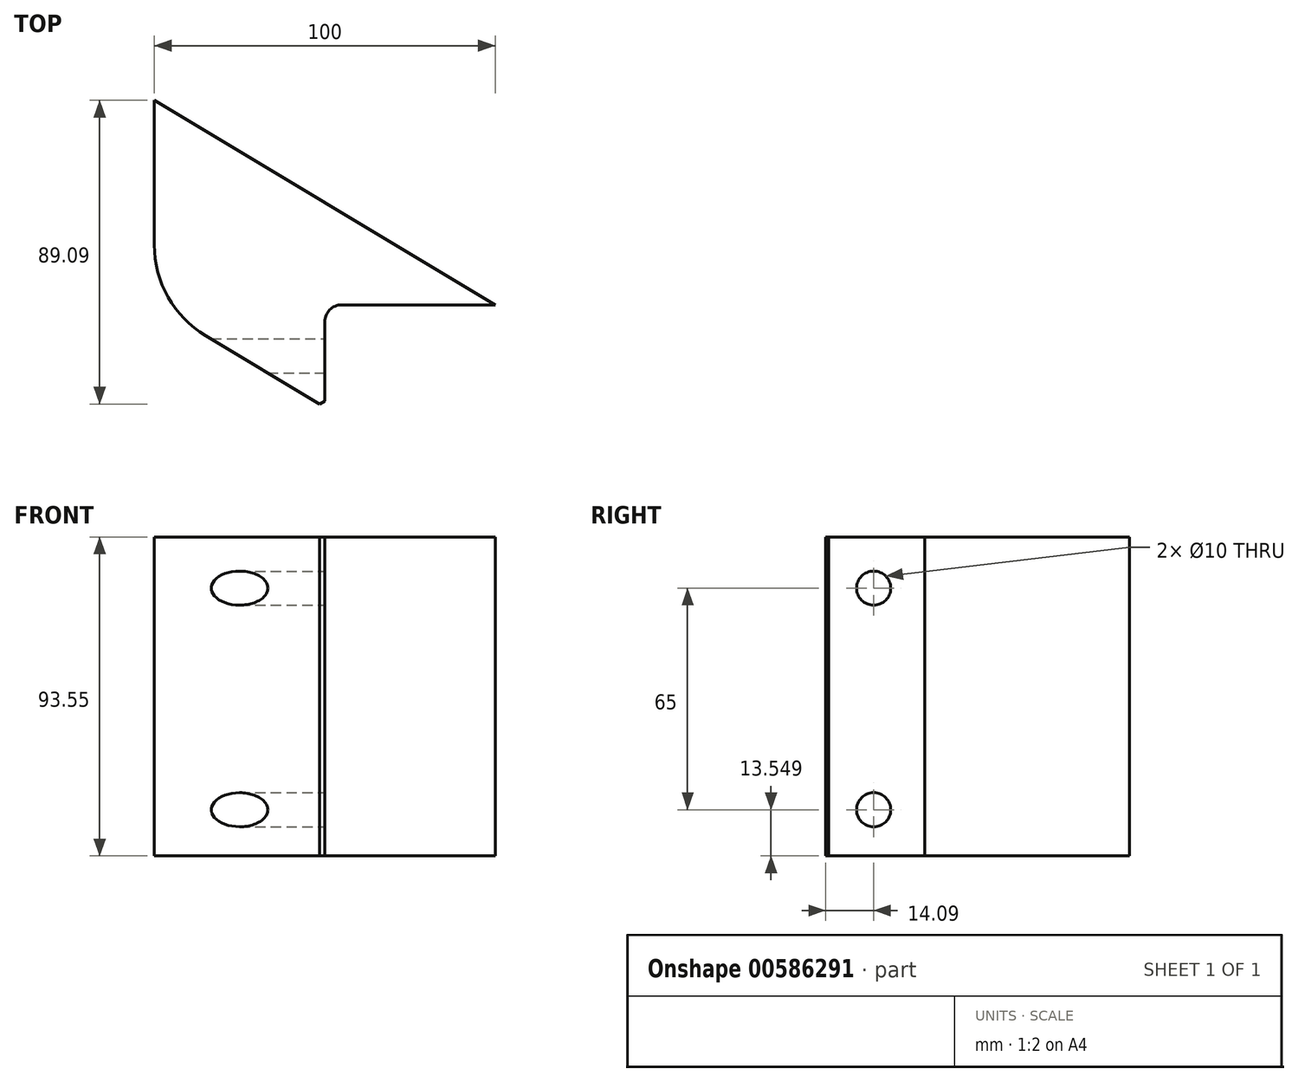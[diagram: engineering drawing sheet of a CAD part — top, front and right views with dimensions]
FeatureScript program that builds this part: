
annotation { "Feature Type Name" : "Feature", "Feature Type Description" : "" }
export const myFeature = defineFeature(function(context is Context, id is Id, definition is map)
    precondition{}
    {
        {
            var Q0;
            Q0=qCreatedBy(makeId("Top.planeOp"),FACE);
            var sketch = newSketch(context, id + "F0", { "sketchPlane" : qUnion([Q0])});
            skLineSegment(sketch, "E0", {"start": v(-50, 50) * mm, "end": v(-50, -10) * mm});
            skLineSegment(sketch, "E1", {"start": v(-50, -10) * mm, "end": v(0, -40) * mm});
            skLineSegment(sketch, "E2", {"start": v(0, -10) * mm, "end": v(0, -40) * mm});
            skLineSegment(sketch, "E3", {"start": v(0, -10) * mm, "end": v(50, -10) * mm});
            skLineSegment(sketch, "E4", {"start": v(50, -10) * mm, "end": v(-50, 50) * mm});
            skSolve(sketch);
        }
        {
            var Q0;
            Q0 = qSketchRegion(id + "F0", true);
            extrude(context, id + "F1", {"entities" : qUnion([Q0]), "depth" : 93.55 * mm, "offsetDistance" : 25 * mm});
        }
        {
            var Q0;
            Q0=makeQuery(id+"F1.opExtrude","SWEPT_FACE",FACE,{"disambiguationData":[OSD([sQuery(id+"F0.wireOp",EDGE,"E2")])]});
            var sketch = newSketch(context, id + "F2", { "sketchPlane" : qUnion([Q0])});
            skPoint(sketch, "E5", {"position": v(-25, 78.55) * mm});
            skPoint(sketch, "E6", {"position": v(-25, 13.55) * mm});
            skSolve(sketch);
        }
        {
            var Q0;
            Q0=sQuery(id+"F2.wireOp",VERTEX,"E5");
            var Q1;
            Q1=sQuery(id+"F2.wireOp",VERTEX,"E6");
            var Q2;
            Q2=makeQuery(id+"F1.opExtrude","SWEPT_BODY",BODY,{"disambiguationData":[OSD([sQuery(id+"F0.wireOp",EDGE,"E0"),sQuery(id+"F0.wireOp",EDGE,"E1"),sQuery(id+"F0.wireOp",EDGE,"E2"),sQuery(id+"F0.wireOp",EDGE,"E3"),sQuery(id+"F0.wireOp",EDGE,"E4")])]});
            hole(context, id + "F3", {"style" : HoleStyle.SIMPLE, "endStyle" : HoleEndStyle.THROUGH, "holeDiameter" : 10 * mm, "majorDiameter" : 5 * mm, "isTappedThrough" : true, "tappedDepth" : 12 * mm, "tapClearance" : 3, "locations" : qUnion([Q0, Q1]), "scope" : qUnion([Q2])});
        }
        {
            var Q0;
            Q0=makeQuery(id+"F1.opExtrude","SWEPT_EDGE",EDGE,{"disambiguationData":[OSD([sQuery(id+"F0.wireOp",EDGE,"E0"),sQuery(id+"F0.wireOp",EDGE,"E1")])]});
            fillet(context, id + "F4", {"entities" : qUnion([Q0]), "radius" : 31 * mm, "tangentPropagation" : true, "allowEdgeOverflow" : false});
        }
        {
            var Q0;
            Q0=makeQuery(id+"F1.opExtrude","SWEPT_EDGE",EDGE,{"disambiguationData":[OSD([sQuery(id+"F0.wireOp",EDGE,"E1"),sQuery(id+"F0.wireOp",EDGE,"E2")])]});
            chamfer(context, id + "F5", {"entities" : qUnion([Q0]), "width" : 1 * mm, "tangentPropagation" : true});
        }
        {
            var Q0;
            Q0=makeQuery(id+"F1.opExtrude","SWEPT_EDGE",EDGE,{"disambiguationData":[OSD([sQuery(id+"F0.wireOp",EDGE,"E2"),sQuery(id+"F0.wireOp",EDGE,"E3")])]});
            fillet(context, id + "F6", {"entities" : qUnion([Q0]), "radius" : 5 * mm, "tangentPropagation" : true, "allowEdgeOverflow" : false});
        }
    });
